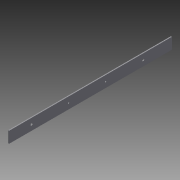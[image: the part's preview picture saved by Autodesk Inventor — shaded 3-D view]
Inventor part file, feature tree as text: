
AUTODESK INVENTOR PART (.ipt)
format: ipt  version: 2015 (Build 190159000, 159)  size: 83,968 bytes
history: native  units: in
note: dims shown in document units (in); Inventor stores cm internally (conversion verified against a paired STEP export)
features: extrude x1, sketch x1
ambient origin geometry x8: Origin, YZ Plane, XZ Plane, XY Plane, X Axis, Y Axis, Z Axis, Center Point
bodies: Solid1 (feature_tree)
feature tree (2):
  extrude  "Extrusion1"  Depth=21.6875in
  sketch  "Sketch1"  dims[d0=1.5in d1=21.6875in d2=3.0in d3=7.9375in d4=12.875in d5=17.875in d6=0.19in d7=0.19in d8=0.3125in d9=0.3125in d10=0.13in d11=0.0in]
